# Revit family: 6kt.Schraube DIN EN ISO 4017, fvz
name_source: partatom
category: HLS-Bauteile
revit_build: Autodesk Revit 2018 (Build: 20190510_1515(x64)
units: mm (PartAtom-declared; Revit-internal decimal feet)

## family parameters
Arbeitsebenenbasiert = Ja
Beim Laden mit Abzugskörper schneiden = Nein
Bemaßung runder Anschluss = Durchmesser verwenden
Gemeinsam genutzt = Ja
Immer vertikal = Nein
Raumberechnungspunkt = Nein
Teiletyp = Normal

## types (5) — shared parameters
Fabrikat = MEFA
Kurztext1 = Sechskantschraube EN ISO 4017
Vorgabe-Ansicht = 1219 mm

## per-type parameters (varying)
| type | Artikelnummer | EAN | Gewicht | Gewicht pro Bauteil | H | Kurztext2 | L | R | d2 |
| M10x 25 SW17, fvz | 3205251/fvz | 4250928456434 | 0.03 kg | 0.03 kg | 6 mm  [stored 0.019685 ft] | M10 x 25 mm fvz FK 8.8 | 25 mm  [stored 0.082021 ft] | 9 mm  [stored 0.0295276 ft] | 4 mm  [stored 0.0131234 ft] |
| M12x 25 SW19, fvz | 3206591/fvz | 4250928457110 | 0.04 kg | 0.04 kg | 8 mm  [stored 0.0262467 ft] | M12 x 25 mm fvz FK 8.8 | 25 mm  [stored 0.082021 ft] | 10 mm  [stored 0.0328084 ft] | 5 mm  [stored 0.0164042 ft] |
| M12x 40 SW19, fvz | 3206606/fvz | 4250928457127 | 0.05 kg | 0.05 kg | 8 mm  [stored 0.0262467 ft] | M12 x 40 mm fvz FK 8.8 | 40 mm  [stored 0.131234 ft] | 10 mm  [stored 0.0328084 ft] | 5 mm  [stored 0.0164042 ft] |
| M12x 55 SW19, fvz | 320660655/fvz | 4250928457134 | 0.06 kg | 0.06 kg | 8 mm  [stored 0.0262467 ft] | M12 x 55 mm fvz FK 8.8 | 55 mm  [stored 0.180446 ft] | 10 mm  [stored 0.0328084 ft] | 5 mm  [stored 0.0164042 ft] |
| M16x 60 SW24, fvz | 3207660/fvz | 4250928457288 | 0.13 kg | 0.13 kg | 10 mm  [stored 0.0328084 ft] | M16 x 60 mm fvz FK 8.8 | 60 mm  [stored 0.19685 ft] | 12 mm  [stored 0.0393701 ft] | 7 mm  [stored 0.0229659 ft] |

note: [stored X ft] marks values corroborated as IEEE doubles in the binary element streams (Revit-internal decimal feet)
